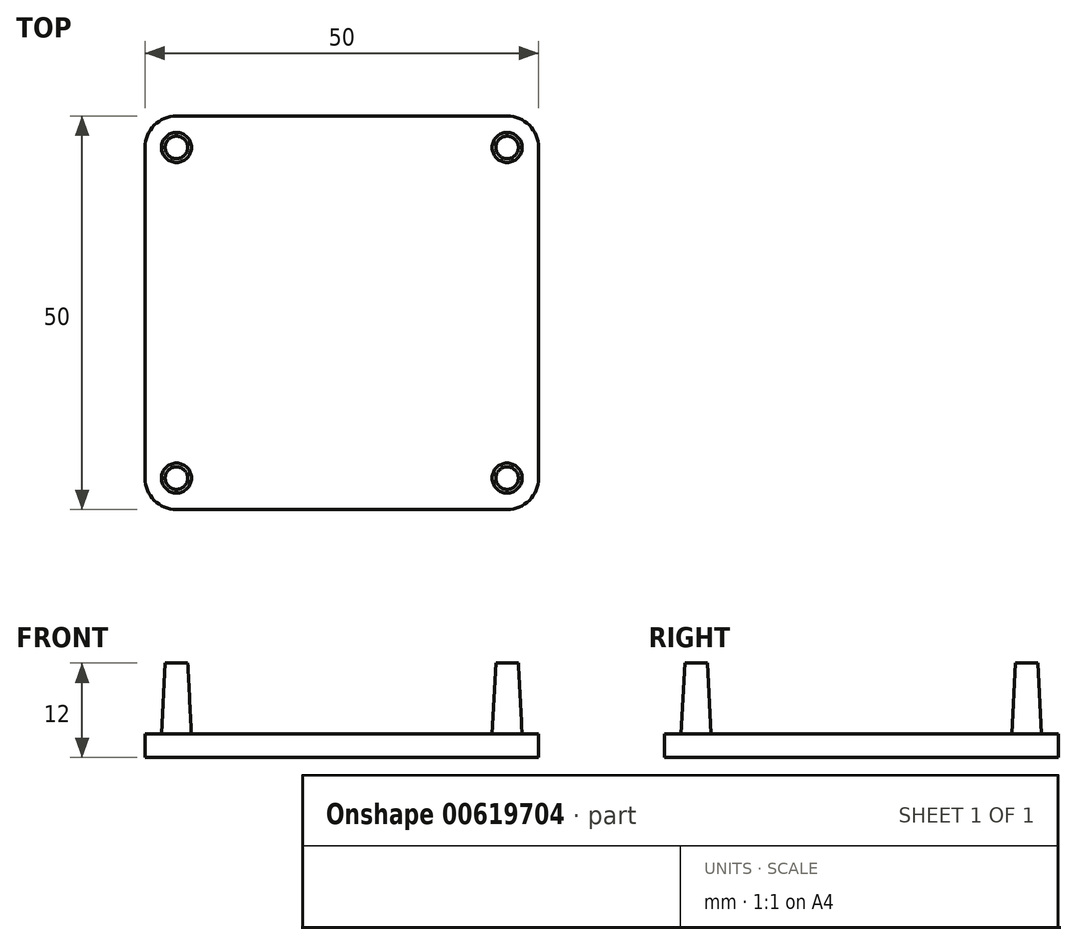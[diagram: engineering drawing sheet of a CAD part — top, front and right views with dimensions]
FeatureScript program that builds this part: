
annotation { "Feature Type Name" : "Feature", "Feature Type Description" : "" }
export const myFeature = defineFeature(function(context is Context, id is Id, definition is map)
    precondition{}
    {
        {
            var Q0;
            Q0=qCreatedBy(makeId("Top.planeOp"),FACE);
            var sketch = newSketch(context, id + "F0", { "sketchPlane" : qUnion([Q0])});
            skLineSegment(sketch, "E0.bottom", {"start": v(-21, 25) * mm, "end": v(21, 25) * mm});
            skLineSegment(sketch, "E0.top", {"start": v(-21, -25) * mm, "end": v(21, -25) * mm});
            skLineSegment(sketch, "E0.left", {"start": v(-25, 21) * mm, "end": v(-25, -21) * mm});
            skLineSegment(sketch, "E0.right", {"start": v(25, 21) * mm, "end": v(25, -21) * mm});
            skPoint(sketch, "E0.middle", {"position": v(0, 0) * mm});
            skPoint(sketch, "E1.visualSharp", {"position": v(-25, 25) * mm});
            skArc(sketch, "E1.filletArc", {"start": v(-21, 25) * mm, "mid": v(-23.83, 23.83) * mm, "end": v(-25, 21) * mm});
            skPoint(sketch, "E2.visualSharp", {"position": v(25, 25) * mm});
            skArc(sketch, "E2.filletArc", {"start": v(25, 21) * mm, "mid": v(23.83, 23.83) * mm, "end": v(21, 25) * mm});
            skPoint(sketch, "E3.visualSharp", {"position": v(25, -25) * mm});
            skArc(sketch, "E3.filletArc", {"start": v(21, -25) * mm, "mid": v(23.83, -23.83) * mm, "end": v(25, -21) * mm});
            skPoint(sketch, "E4.visualSharp", {"position": v(-25, -25) * mm});
            skArc(sketch, "E4.filletArc", {"start": v(-25, -21) * mm, "mid": v(-23.83, -23.83) * mm, "end": v(-21, -25) * mm});
            skSolve(sketch);
        }
        {
            var Q0;
            Q0=makeQuery(id+"F0.imprint","IMPRINT",FACE,{"disambiguationData":[TD([[makeQuery(id+"F0.imprint","IMPRINT",EDGE,{"derivedFrom":sQuery(id+"F0.wireOp",EDGE,"E0.bottom")}),-1.0]])]});
            extrude(context, id + "F1", {"entities" : qUnion([Q0]), "depth" : 3 * mm, "offsetDistance" : 25 * mm});
        }
        {
            var Q0;
            Q0=makeQuery(id+"F1.opExtrude","CAP_FACE",FACE,{"disambiguationData":[OSD([sQuery(id+"F0.wireOp",EDGE,"E0.bottom"),sQuery(id+"F0.wireOp",EDGE,"E0.top"),sQuery(id+"F0.wireOp",EDGE,"E0.left"),sQuery(id+"F0.wireOp",EDGE,"E0.right"),sQuery(id+"F0.wireOp",EDGE,"E1.filletArc"),sQuery(id+"F0.wireOp",EDGE,"E2.filletArc"),sQuery(id+"F0.wireOp",EDGE,"E3.filletArc"),sQuery(id+"F0.wireOp",EDGE,"E4.filletArc")])],"isStart":false});
            var sketch = newSketch(context, id + "F2", { "sketchPlane" : qUnion([Q0])});
            skCircle(sketch, "E5", {"center": v(-21, 21) * mm, "radius": 1.9 * mm});
            skCircle(sketch, "E6", {"center": v(21, 21) * mm, "radius": 1.9 * mm});
            skCircle(sketch, "E7", {"center": v(21, -21) * mm, "radius": 1.9 * mm});
            skCircle(sketch, "E8", {"center": v(-21, -21) * mm, "radius": 1.9 * mm});
            skSolve(sketch);
        }
        {
            var Q0;
            Q0 = qSketchRegion(id + "F2", true);
            extrude(context, id + "F3", {"entities" : qUnion([Q0]), "operationType" : NewBodyOperationType.ADD, "depth" : 9 * mm, "offsetDistance" : 25 * mm, "hasDraft" : true, "draftAngle" : 3 * degree, "draftPullDirection" : true});
        }
    });
